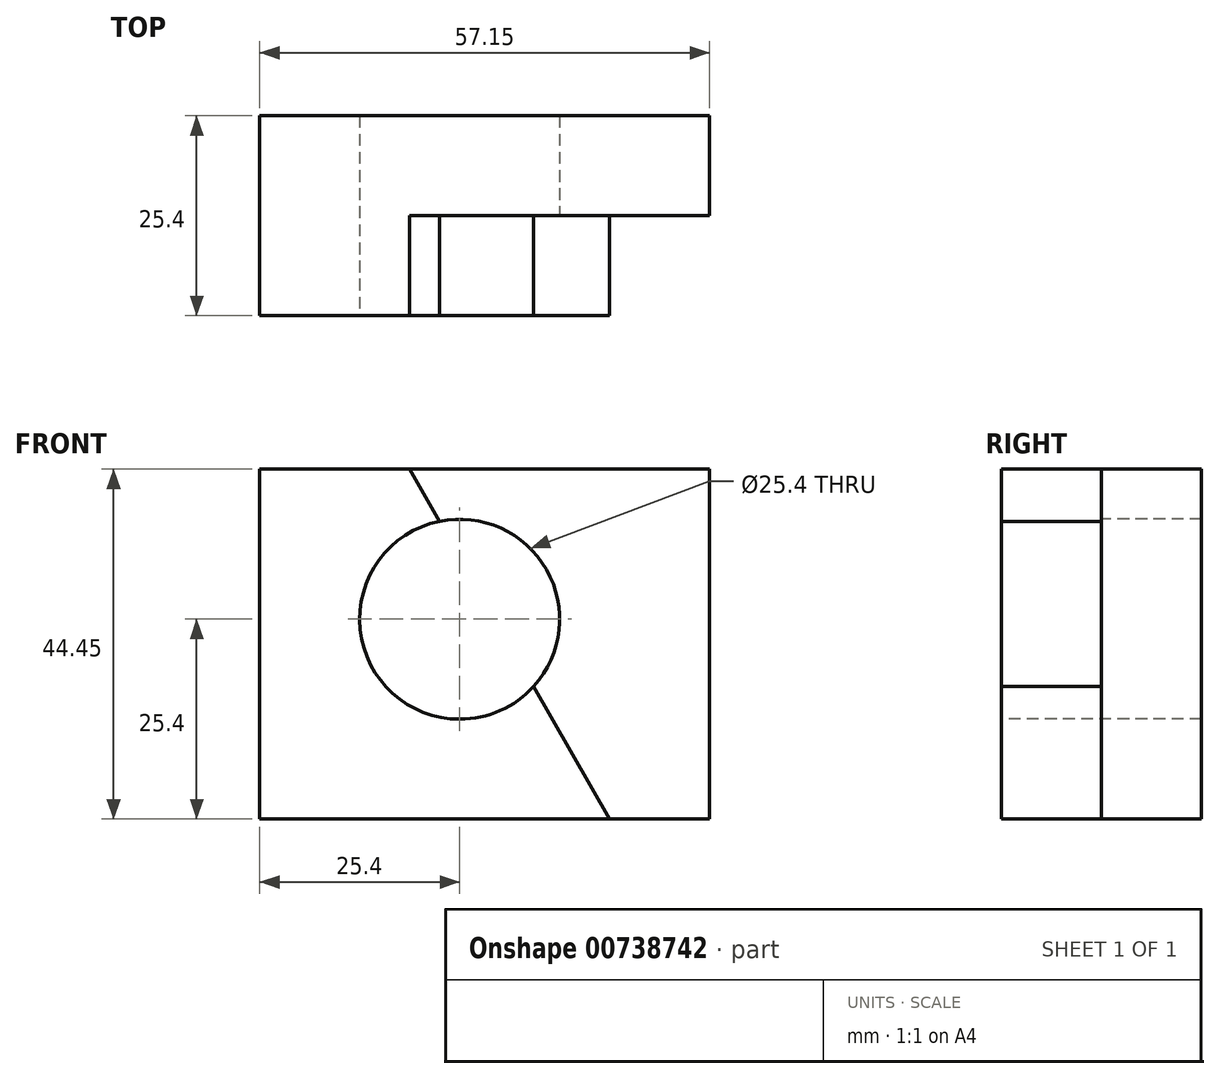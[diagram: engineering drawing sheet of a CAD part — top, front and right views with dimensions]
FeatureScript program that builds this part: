
annotation { "Feature Type Name" : "Feature", "Feature Type Description" : "" }
export const myFeature = defineFeature(function(context is Context, id is Id, definition is map)
    precondition{}
    {
        {
            var Q0;
            Q0=qCreatedBy(makeId("Front.planeOp"),FACE);
            var sketch = newSketch(context, id + "F0", { "sketchPlane" : qUnion([Q0])});
            skLineSegment(sketch, "E0", {"start": v(0, 0) * mm, "end": v(57.15, 0) * mm});
            skLineSegment(sketch, "E1", {"start": v(57.15, 0) * mm, "end": v(57.15, 44.45) * mm});
            skLineSegment(sketch, "E2", {"start": v(57.15, 44.45) * mm, "end": v(0, 44.45) * mm});
            skLineSegment(sketch, "E3", {"start": v(0, 44.45) * mm, "end": v(0, 0) * mm});
            skSolve(sketch);
        }
        {
            var Q0;
            Q0 = qSketchRegion(id + "F0", true);
            extrude(context, id + "F1", {"entities" : qUnion([Q0]), "depth" : 25.4 * mm, "offsetDistance" : 25.4 * mm});
        }
        {
            var Q0;
            Q0=makeQuery(id+"F1.opExtrude","CAP_FACE",FACE,{"disambiguationData":[OSD([sQuery(id+"F0.wireOp",EDGE,"E0"),sQuery(id+"F0.wireOp",EDGE,"E1"),sQuery(id+"F0.wireOp",EDGE,"E2"),sQuery(id+"F0.wireOp",EDGE,"E3")])],"isStart":false});
            var sketch = newSketch(context, id + "F2", { "sketchPlane" : qUnion([Q0])});
            skLineSegment(sketch, "E4", {"start": v(25.4, 44.45) * mm, "end": v(25.4, 0) * mm});
            skLineSegment(sketch, "E5", {"start": v(0, 25.4) * mm, "end": v(57.15, 25.4) * mm});
            skCircle(sketch, "E6", {"center": v(25.4, 25.4) * mm, "radius": 12.7 * mm});
            skSolve(sketch);
        }
        {
            var Q0;
            Q0 = qSketchRegion(id + "F2", true);
            extrude(context, id + "F3", {"entities" : qUnion([Q0]), "operationType" : NewBodyOperationType.REMOVE, "endBound" : BoundingType.THROUGH_ALL, "oppositeDirection" : true, "depth" : 25.4 * mm, "offsetDistance" : 25.4 * mm});
        }
        {
            var Q0;
            Q0=makeQuery(id+"F1.opExtrude","CAP_FACE",FACE,{"disambiguationData":[OSD([sQuery(id+"F0.wireOp",EDGE,"E0"),sQuery(id+"F0.wireOp",EDGE,"E1"),sQuery(id+"F0.wireOp",EDGE,"E2"),sQuery(id+"F0.wireOp",EDGE,"E3")])],"isStart":false});
            var sketch = newSketch(context, id + "F4", { "sketchPlane" : qUnion([Q0])});
            skLineSegment(sketch, "E7", {"start": v(19.05, 44.45) * mm, "end": v(44.45, 0) * mm});
            skLineSegment(sketch, "E8", {"start": v(19.05, 44.45) * mm, "end": v(57.15, 44.45) * mm});
            skLineSegment(sketch, "E9", {"start": v(57.15, 44.45) * mm, "end": v(57.15, 0) * mm});
            skLineSegment(sketch, "E10", {"start": v(57.15, 0) * mm, "end": v(44.45, 0) * mm});
            skSolve(sketch);
        }
        {
            var Q0;
            {var subQ0=sQuery(id+"F4.wireOp",EDGE,"E8");Q0=makeQuery(id+"F4.imprint","IMPRINT",FACE,{"disambiguationData":[TD([[makeQuery(id+"F4.imprint","IMPRINT",EDGE,{"derivedFrom":subQ0}),1.0]])]});}
            extrude(context, id + "F5", {"entities" : qUnion([Q0]), "operationType" : NewBodyOperationType.REMOVE, "oppositeDirection" : true, "depth" : 12.7 * mm, "offsetDistance" : 25.4 * mm});
        }
    });
